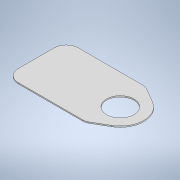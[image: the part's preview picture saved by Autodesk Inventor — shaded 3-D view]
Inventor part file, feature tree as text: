
AUTODESK INVENTOR PART (.ipt)
format: ipt  version: 2021 (Build 250183000, 183)  size: 119,296 bytes
history: native  units: mm
features: extrude x1, sketch x1
ambient origin geometry x8: Origin, YZ Plane, XZ Plane, XY Plane, X Axis, Y Axis, Z Axis, Center Point
bodies: Solid1 (feature_tree)
feature tree (2):
  extrude  "Extrusion1"  Depth=4.0mm
  sketch  "Sketch1"  dims[d0=11.4mm d1=9.0mm d2=12.65mm d5=25.0mm d6=5.0mm d8=0.5mm d9=0.0mm d10=25.0mm d11=19.6mm d12=4.0mm]
